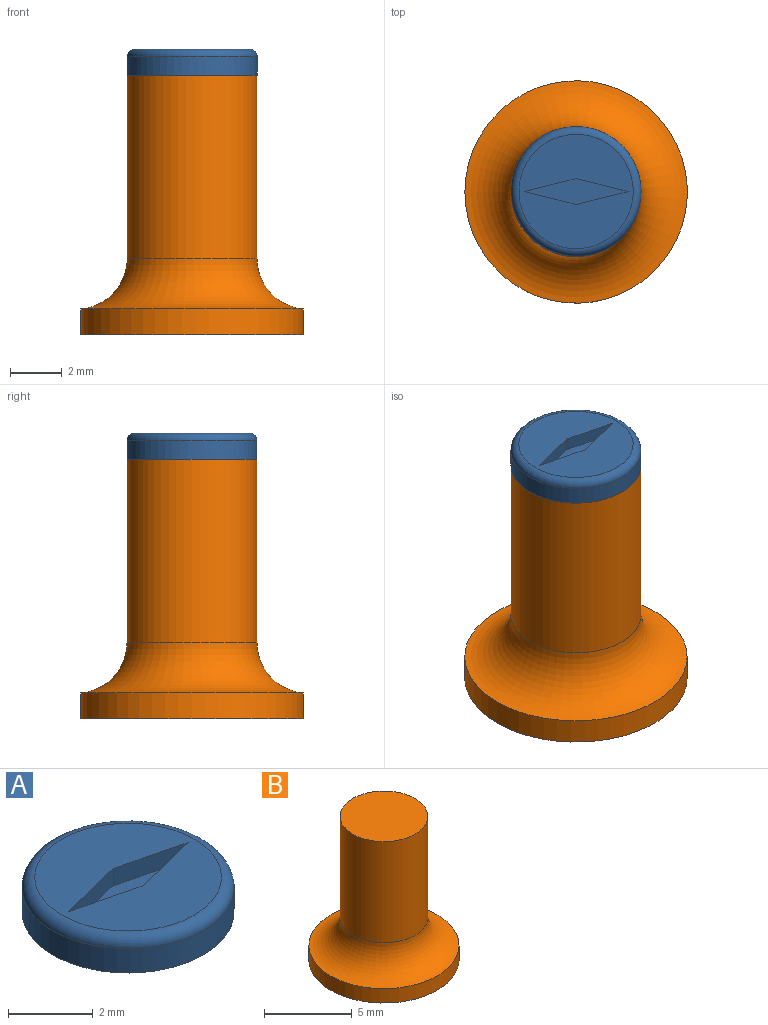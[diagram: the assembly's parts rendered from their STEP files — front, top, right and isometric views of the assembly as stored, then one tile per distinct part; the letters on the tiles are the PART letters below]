
ASSEMBLY  parts=2 mates=1
PART A: 9 faces, bbox 5.4x5.4x1 mm
  f0: plane 4.4x4.4mm, normal (0,0,1), area 13.2mm2, adj f3,f4,f5,f6,f7
  f1: plane 5x5mm, normal (0,0,-1), area 19.6mm2, adj f2
  f2: cylinder r=2.5mm len=5mm, axis (0,0,1), area 11mm2, adj f1,f3
  f3: torus R=2.2mm, axis (0,0,1), area 7.1mm2, adj f0,f2
  f4: plane 2x0.5mm, normal (0.24,-0.97,0), area 1mm2, adj f0,f5,f7,f8
  f5: plane 2x0.5mm, normal (0.24,0.97,0), area 1mm2, adj f0,f4,f6,f8
  f6: plane 2x0.5mm, normal (-0.24,0.97,0), area 1mm2, adj f0,f5,f7,f8
  f7: plane 2x0.5mm, normal (-0.24,-0.97,0), area 1mm2, adj f0,f4,f6,f8
  f8: plane 4x1mm, normal (0,0,1), area 2mm2, adj f4,f5,f6,f7
PART B: 5 faces, bbox 9.6x9.6x10 mm
  f0: torus R=4.45mm, axis (0,0,-1), area 57.1mm2, adj f1,f4
  f1: cylinder r=2.5mm len=7.05mm, axis (0,0,-1), area 110.8mm2, adj f0,f2
  f2: plane 5x5mm, normal (0,0,1), area 19.6mm2, adj f1
  f3: plane 8.56x8.56mm, normal (0,0,-1), area 57.5mm2, adj f4
  f4: cylinder r=4.28mm len=8.56mm, axis (0,0,-1), area 26.9mm2, adj f0,f3
PLACE A t=(0,0,10)mm
PLACE B at identity fixed
MATE fastened A.f2 <-> B.f0  axis (0,0,-1) through (0,0,9)mm
